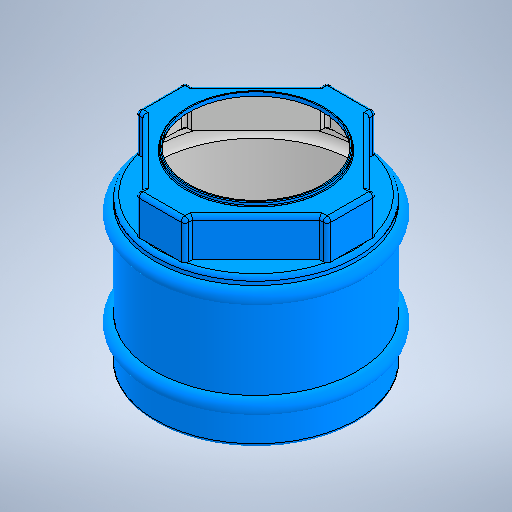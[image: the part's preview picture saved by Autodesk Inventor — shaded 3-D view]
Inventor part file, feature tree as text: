
AUTODESK INVENTOR PART (.ipt)
format: ipt  version: 2025.1 (Build 291241020, 241B)  size: 543,232 bytes
history: native  units: mm
features: projected_geometry x5, sketch x3, extrude x2, fillet x2, revolve x1, shell x1
ambient origin geometry x8: Origin, YZ Plane, XZ Plane, XY Plane, X Axis, Y Axis, Z Axis, Center Point
bodies: Body1 (feature_tree)
feature tree (14):
  extrude  "Extrusion4"  Depth=130.0mm
  revolve  "Revolution1"  [1 undecoded]
  fillet  "Fillet1"  Radius=490.0mm
  fillet  "Fillet2"  Radius=40.0mm
  extrude  "Extrusion5"  Depth=2.0mm
  shell  "Shell2"  Thickness=360.0mm
  sketch  "Sketch5"  dims[d11=520.0mm d12=130.0mm]
  sketch  "Sketch7"  dims[d13=45.0deg d14=210.0mm d15=490.0mm d16=0.0mm d18=40.0mm]
  projected_geometry  "Projected Loop6"
  projected_geometry  "Projected Loop7"
  projected_geometry  "Projected Loop8"
  projected_geometry  "Projected Loop9"
  sketch  "Sketch8"  dims[d19=100.0mm d20=250.0mm d21=360.0mm d22=10.0mm d23=100.0mm d25=360.0deg d26=10.0mm d27=2.0mm d28=3.0mm d29=10.0mm d30=0.0mm d32=570.0mm d33=2.0mm]
  projected_geometry  "Projected Loop10"
note: 1 required parameter value undecoded (feature->parameter linkage not recoverable at this tier; creation-order binding heuristic only, values carry confidence <= 0.55)
